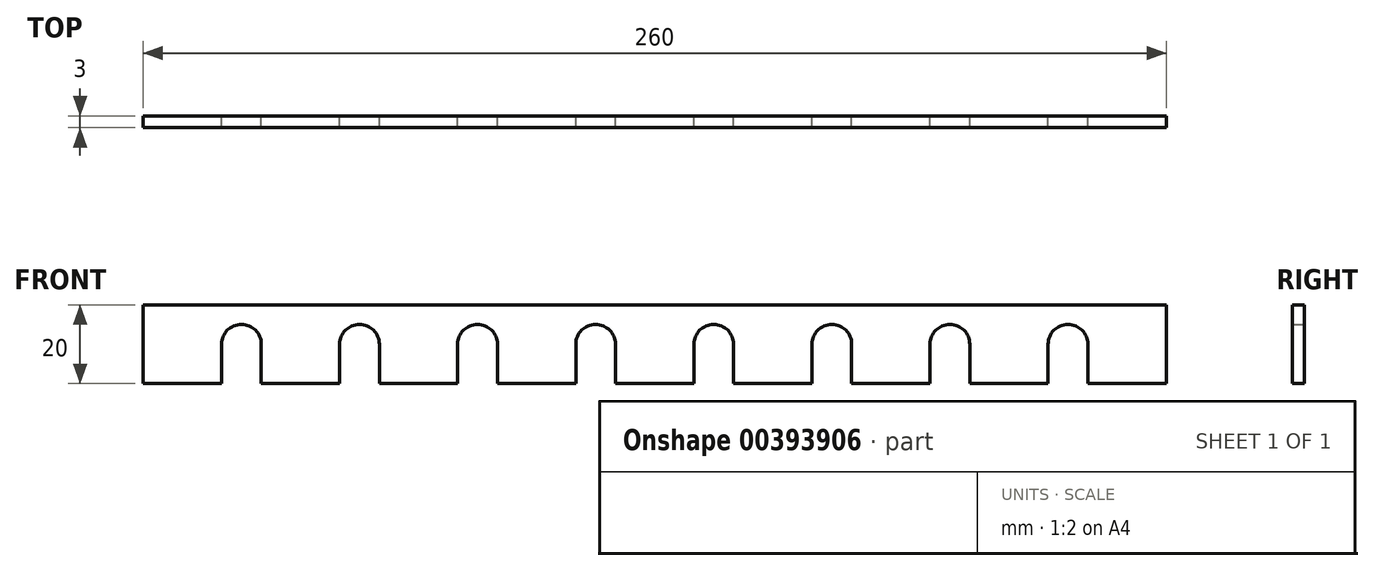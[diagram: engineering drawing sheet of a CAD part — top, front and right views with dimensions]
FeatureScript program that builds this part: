
annotation { "Feature Type Name" : "Feature", "Feature Type Description" : "" }
export const myFeature = defineFeature(function(context is Context, id is Id, definition is map)
    precondition{}
    {
        {
            var Q0;
            Q0=qCreatedBy(makeId("Front.planeOp"),FACE);
            var sketch = newSketch(context, id + "F0", { "sketchPlane" : qUnion([Q0])});
            skLineSegment(sketch, "E0.bottom", {"start": v(130, 10) * mm, "end": v(-130, 10) * mm});
            skLineSegment(sketch, "E0.top", {"start": v(130, -10) * mm, "end": v(-130, -10) * mm});
            skLineSegment(sketch, "E0.left", {"start": v(130, 10) * mm, "end": v(130, -10) * mm});
            skLineSegment(sketch, "E0.right", {"start": v(-130, 10) * mm, "end": v(-130, -10) * mm});
            skPoint(sketch, "E0.middle", {"position": v(0, 0) * mm});
            skArc(sketch, "E1", {"start": v(-99.95, 0) * mm, "mid": v(-105, 5.05) * mm, "end": v(-110.05, 0) * mm});
            skLineSegment(sketch, "E2", {"start": v(-99.95, 0) * mm, "end": v(-99.95, -10) * mm});
            skLineSegment(sketch, "E3", {"start": v(-110.05, 0) * mm, "end": v(-110.05, -10) * mm});
            skArc(sketch, "E4.1.0.0", {"start": v(-69.95, 0) * mm, "mid": v(-75, 5.05) * mm, "end": v(-80.05, 0) * mm});
            skLineSegment(sketch, "E4.1.0.1", {"start": v(-69.95, 0) * mm, "end": v(-69.95, -10) * mm});
            skLineSegment(sketch, "E4.1.0.2", {"start": v(-80.05, 0) * mm, "end": v(-80.05, -10) * mm});
            skArc(sketch, "E4.2.0.0", {"start": v(-39.95, 0) * mm, "mid": v(-45, 5.05) * mm, "end": v(-50.05, 0) * mm});
            skLineSegment(sketch, "E4.2.0.1", {"start": v(-39.95, 0) * mm, "end": v(-39.95, -10) * mm});
            skLineSegment(sketch, "E4.2.0.2", {"start": v(-50.05, 0) * mm, "end": v(-50.05, -10) * mm});
            skArc(sketch, "E4.3.0.0", {"start": v(-9.95, 0) * mm, "mid": v(-15, 5.05) * mm, "end": v(-20.05, 0) * mm});
            skLineSegment(sketch, "E4.3.0.1", {"start": v(-9.95, 0) * mm, "end": v(-9.95, -10) * mm});
            skLineSegment(sketch, "E4.3.0.2", {"start": v(-20.05, 0) * mm, "end": v(-20.05, -10) * mm});
            skArc(sketch, "E4.4.0.0", {"start": v(20.05, 0) * mm, "mid": v(15, 5.05) * mm, "end": v(9.95, 0) * mm});
            skLineSegment(sketch, "E4.4.0.1", {"start": v(20.05, 0) * mm, "end": v(20.05, -10) * mm});
            skLineSegment(sketch, "E4.4.0.2", {"start": v(9.95, 0) * mm, "end": v(9.95, -10) * mm});
            skArc(sketch, "E4.5.0.0", {"start": v(50.05, 0) * mm, "mid": v(45, 5.05) * mm, "end": v(39.95, 0) * mm});
            skLineSegment(sketch, "E4.5.0.1", {"start": v(50.05, 0) * mm, "end": v(50.05, -10) * mm});
            skLineSegment(sketch, "E4.5.0.2", {"start": v(39.95, 0) * mm, "end": v(39.95, -10) * mm});
            skArc(sketch, "E4.6.0.0", {"start": v(80.05, 0) * mm, "mid": v(75, 5.05) * mm, "end": v(69.95, 0) * mm});
            skLineSegment(sketch, "E4.6.0.1", {"start": v(80.05, 0) * mm, "end": v(80.05, -10) * mm});
            skLineSegment(sketch, "E4.6.0.2", {"start": v(69.95, 0) * mm, "end": v(69.95, -10) * mm});
            skArc(sketch, "E4.7.0.0", {"start": v(110.05, 0) * mm, "mid": v(105, 5.05) * mm, "end": v(99.95, 0) * mm});
            skLineSegment(sketch, "E4.7.0.1", {"start": v(110.05, 0) * mm, "end": v(110.05, -10) * mm});
            skLineSegment(sketch, "E4.7.0.2", {"start": v(99.95, 0) * mm, "end": v(99.95, -10) * mm});
            skLineSegment(sketch, "E4.direction1", {"start": v(-110.05, 0) * mm, "end": v(-80.05, 0) * mm, "construction": true});
            skSolve(sketch);
        }
        {
            var Q0;
            Q0=makeQuery(id+"F0.imprint","IMPRINT",FACE,{"disambiguationData":[TD([[makeQuery(id+"F0.imprint","IMPRINT",EDGE,{"derivedFrom":sQuery(id+"F0.wireOp",EDGE,"E0.bottom")}),1.0]])]});
            extrude(context, id + "F1", {"entities" : qUnion([Q0]), "depth" : 3 * mm, "offsetDistance" : 25 * mm});
        }
    });
